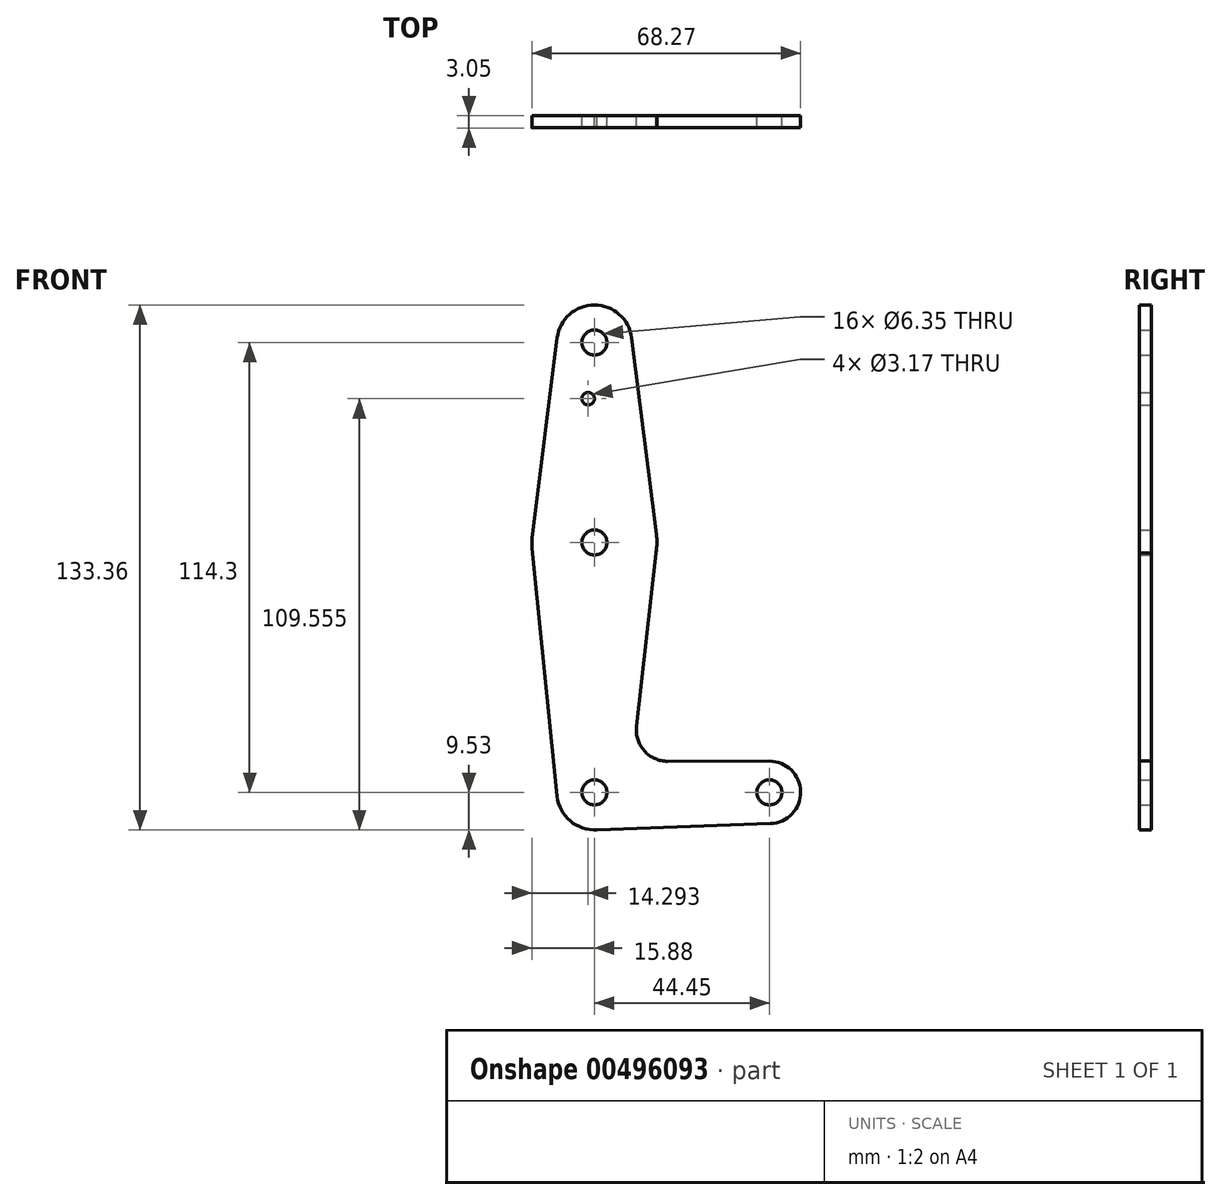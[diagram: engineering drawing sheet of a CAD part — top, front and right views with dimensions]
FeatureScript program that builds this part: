
annotation { "Feature Type Name" : "Feature", "Feature Type Description" : "" }
export const myFeature = defineFeature(function(context is Context, id is Id, definition is map)
    precondition{}
    {
        {
            var Q0;
            Q0=qCreatedBy(makeId("Front.planeOp"),FACE);
            var sketch = newSketch(context, id + "F0", { "sketchPlane" : qUnion([Q0])});
            skLineSegment(sketch, "E0", {"start": v(0, 114.3) * mm, "end": v(0, 0) * mm, "construction": true});
            skLineSegment(sketch, "E1", {"start": v(0, 0) * mm, "end": v(44.45, 0) * mm, "construction": true});
            skCircle(sketch, "E2", {"center": v(0, 114.3) * mm, "radius": 9.53 * mm});
            skCircle(sketch, "E3", {"center": v(0, 63.5) * mm, "radius": 15.88 * mm});
            skCircle(sketch, "E4", {"center": v(0, 0) * mm, "radius": 9.53 * mm});
            skCircle(sketch, "E5", {"center": v(44.45, 0) * mm, "radius": 7.94 * mm});
            skLineSegment(sketch, "E6", {"start": v(-9.45, 115.5) * mm, "end": v(-15.75, 65.48) * mm});
            skLineSegment(sketch, "E7", {"start": v(9.45, 115.5) * mm, "end": v(15.75, 65.48) * mm});
            skLineSegment(sketch, "E8", {"start": v(0, -9.52) * mm, "end": v(44.73, -7.93) * mm});
            skCircle(sketch, "E9", {"center": v(0, 114.3) * mm, "radius": 3.18 * mm});
            skCircle(sketch, "E10", {"center": v(0, 63.5) * mm, "radius": 3.18 * mm});
            skCircle(sketch, "E11", {"center": v(0, 0) * mm, "radius": 3.18 * mm});
            skCircle(sketch, "E12", {"center": v(44.45, 0) * mm, "radius": 3.18 * mm});
            skCircle(sketch, "E13", {"center": v(-1.59, 100.03) * mm, "radius": 1.59 * mm});
            skLineSegment(sketch, "E14", {"start": v(-15.8, 61.91) * mm, "end": v(-9.48, -0.95) * mm});
            skLineSegment(sketch, "E15", {"start": v(15.67, 60.83) * mm, "end": v(10.7, 16.74) * mm});
            skLineSegment(sketch, "E16", {"start": v(18.61, 7.9) * mm, "end": v(44.44, 7.94) * mm});
            skArc(sketch, "E17.filletArc", {"start": v(10.7, 16.74) * mm, "mid": v(12.68, 10.55) * mm, "end": v(18.61, 7.9) * mm});
            skLineSegment(sketch, "E18", {"start": v(15.67, 60.83) * mm, "end": v(15.65, 60.83) * mm});
            skLineSegment(sketch, "E19", {"start": v(15.65, 60.83) * mm, "end": v(15.65, 60.83) * mm});
            skLineSegment(sketch, "E20", {"start": v(44.44, 7.94) * mm, "end": v(44.44, 7.94) * mm});
            skSolve(sketch);
        }
        {
            var Q0;
            Q0 = qSketchRegion(id + "F0", true);
            extrude(context, id + "F1", {"entities" : qUnion([Q0]), "depth" : 3.05 * mm});
        }
    });
